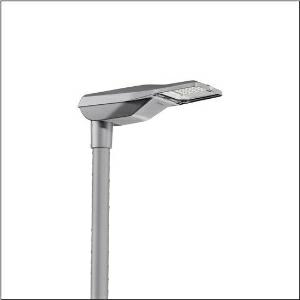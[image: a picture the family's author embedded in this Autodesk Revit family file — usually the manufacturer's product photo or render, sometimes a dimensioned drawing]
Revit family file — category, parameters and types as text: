
# Revit family: streetlight_sl_21_iq_micro___stw1_0a_5xe1e41g08cb_8385
name_source: partatom
category: Lighting Fixtures
units: mm (PartAtom-declared; Revit-internal decimal feet)

## family parameters
Cut with Voids When Loaded = No
Host = Face
Light Source = No
Part Type = Normal
Room Calculation Point = No
Round Connector Dimension = Use Diameter
Shared = No

## types (1)
- --- (1 x LED, 2980 lm, 19.4 W, 4000K)
    Apparent Load = 19 VA
    CIE Flux Codes = 38 75 98 100 100
    Color Rendering = 70
    Color Temperature = 4000K
    Default Elevation = 1800 mm
    Description = Streetlight SL 21 iQ micro, mast luminaire, primary light control with lens, of PMMA, primary optical cover: cover, of toughened safety glass, transparent, light distribution: STW1.0a, light emission: direct distribution, primary light characteristic: asymmetric, installation type: post-top, side-entry, LED, High Power LED, rated luminous flux: 2.980lm, luminous efficacy: 154lm/W, light colour: 740, colour temperature: 4000K, control gear: iQ Street-Remote, control: Street-Remote, Auto-Match, Temp-Guard, Lumen-Switch, Night-Set, Smart-Wire, Light-Fading, Desk-Remote (wireless, voltage-free reading and setting of iQ features in the workshop via application-optimized NFC function/RFID function), optimised constant luminous flux control (CLO 2.0), pre-setting: linear dimming characteristic, mains connection: 220..240V, AC, 50/60Hz, start of lifetime: 19W, end of service life: 20W, reduction: 10W, luminaire housing, of diecast aluminium, powder-coated, Siteco® metallic grey (DB 702S), corrosivity category C5 mid according to DIN EN ISO 12944, please order mast flange separately, inclination adjustable: 0°, 5°, 10°, 15°, sealing non-destructively replaceable, multi-level sealing system, length: 528mm, width: 235mm, height: 110mm, mast flange for spigot size: 42mm (side-entry): 5XC10008XM4, 60/48mm (side-entry/post-top): 5XC10108XM2, 76/60mm (side-entry/post-top): 5XC10108XM1, protection rating (complete): IP66, insulation class (complete): insulation class II (safety insulation), certification: CE, ENEC, ENEC+, VDE, impact resistance: IK10, permissible operating ambient temperature for outdoor applications: -40..+50°C, standard-compliant lighting for roads and squares, packaging unit: 1 piece

Light Distribution: STW1.0a
    Height = 110 mm
    Lamp = 1 x LED
    Lamp Light Flux = 2980 lm
    Lamp Power = 19.4 W
    Lamp count = 1
    Length = 528 mm
    Luminous efficacy = 154 lm/W
    Manufacturer = Siteco
    ModVariant = No
    Model = 5XE1E41G08CB
    Number of Poles = 1
    OnlyDefault = Yes
    Power Factor = 1
    Product Name = Streetlight SL 21 iQ micro | STW1.0a
    Product group = mast luminaire | pylon top
    ProductGroupID = 6100
    Protection Class = Protection class II
    Protection Degree = IP 66
    RLX_Detail_Level = 1
    RLX_Emergency_Light_Flux = 0 lm
    RLX_Emergency_Type = 0
    RLX_Emergency_Type_DB = No
    RlxData = <blob elided: 98705 chars, md5=c728d72a>
    Socket = socket
    Standby Power = 0 W
    System Light Flux = 2980 lm
    System Power = 19 W
    Type Comments = factory setting: luminous flux: 100 % | dim-lin: 254 | 387 mA
    Type Image = l_1006881.jpg
    URL = http://relux.com
    VarID = @adj_160267
    Voltage = 0 V
    Weight = 0.00 kg
    Width = 235 mm

## geometry (parser evidence)
native form markers: Blend x4, Sweep x11
no freeform markers — native parametric forms only
